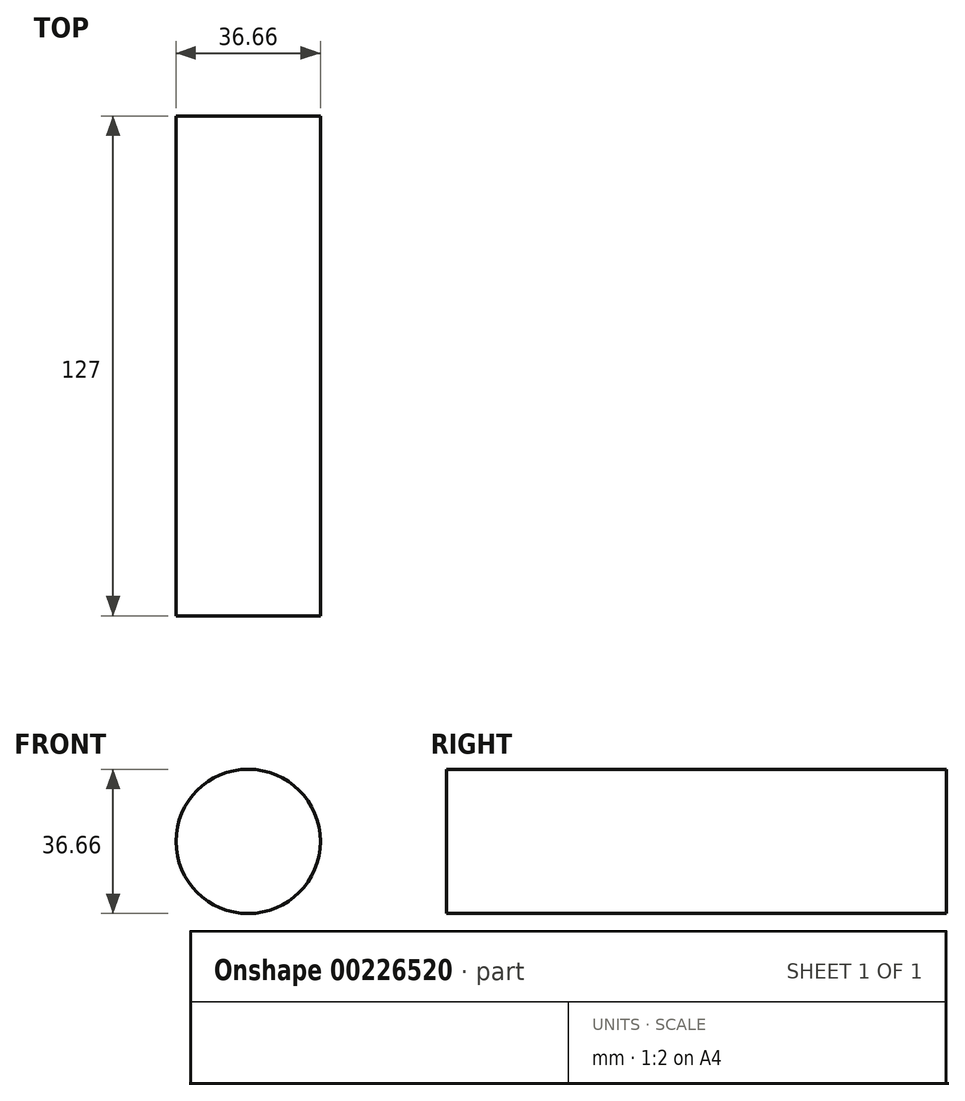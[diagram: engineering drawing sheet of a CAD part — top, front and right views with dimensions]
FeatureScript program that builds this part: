
annotation { "Feature Type Name" : "Feature", "Feature Type Description" : "" }
export const myFeature = defineFeature(function(context is Context, id is Id, definition is map)
    precondition{}
    {
        {
            var Q0;
            Q0=qCreatedBy(makeId("Front.planeOp"),FACE);
            var sketch = newSketch(context, id + "F0", { "sketchPlane" : qUnion([Q0])});
            skCircle(sketch, "E0", {"center": v(55.4, 0) * mm, "radius": 18.33 * mm});
            skSolve(sketch);
        }
        {
            var Q0;
            Q0=sQuery(id+"F0.wireOp",EDGE,"E0");
            extrude(context, id + "F1", {"bodyType" : ToolBodyType.SURFACE, "surfaceEntities" : qUnion([Q0]), "depth" : 127 * mm});
        }
    });
